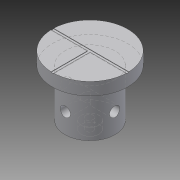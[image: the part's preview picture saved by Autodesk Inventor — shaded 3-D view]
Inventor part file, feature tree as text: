
AUTODESK INVENTOR PART (.ipt)
format: ipt  version: 2013 (Build 170138000, 138)  size: 142,848 bytes
history: native  units: mm
features: extrude x7, sketch x7, plane x4, hole x1, thread x1
ambient origin geometry x8: Origin, YZ Plane, XZ Plane, XY Plane, X Axis, Y Axis, Z Axis, Center Point
bodies: Volumenkörper1 (feature_tree)
feature tree (20):
  extrude  "Extrusion1"  Depth=19.0mm TaperAngle=0.0deg
  extrude  "Extrusion3"  Depth=5.0mm TaperAngle=0.0deg
  extrude  "Extrusion4"  Depth=3.1mm TaperAngle=0.0deg
  plane  "Arbeitsebene1"
  extrude  "Extrusion5"  Depth=8.0mm
  plane  "Arbeitsebene2"
  extrude  "Extrusion6"  Depth=4.0mm
  hole  "Bohrung1"  [1 undecoded]
  thread  "Gewinde1"  [1 undecoded]
  plane  "Arbeitsebene3"
  extrude  "Extrusion7"  Depth=10.0mm TaperAngle=0.0deg
  plane  "Arbeitsebene4"
  extrude  "Extrusion8"  Depth=0.2mm
  sketch  "Skizze1"  dims[d0=19.95mm d2=19.0mm d3=0.0mm]
  sketch  "Skizze3"  dims[d8=30.0mm d10=5.0mm d11=0.0mm]
  sketch  "Skizze4"  dims[d12=7.0mm d14=3.1mm d15=0.0mm]
  sketch  "Skizze5"  dims[d16=4.0mm d18=8.0mm]
  sketch  "Skizze6"  dims[d19=20.0mm d20=0.0mm d21=4.0mm]
  sketch  "Skizze7"  dims[d23=8.0mm d24=10.0mm d25=0.0mm d26=10.0mm d27=10.0mm]
  sketch  "Skizze8"  dims[d28=3.0mm d29=6.0mm d30=4.0mm d31=2.0mm d32=90.0deg d33=4.0mm d34=20.594885mm d35=10.0mm d36=0.0mm d37=0.2mm d39=1.0mm d40=0.5mm d41=0.0mm d42=30.0mm d43=0.0mm d44=0.2mm d45=1.0mm d46=0.5mm d47=0.0mm d48=15.0mm d49=0.0mm]
note: 2 required parameter values undecoded (feature->parameter linkage not recoverable at this tier; creation-order binding heuristic only, values carry confidence <= 0.55)
